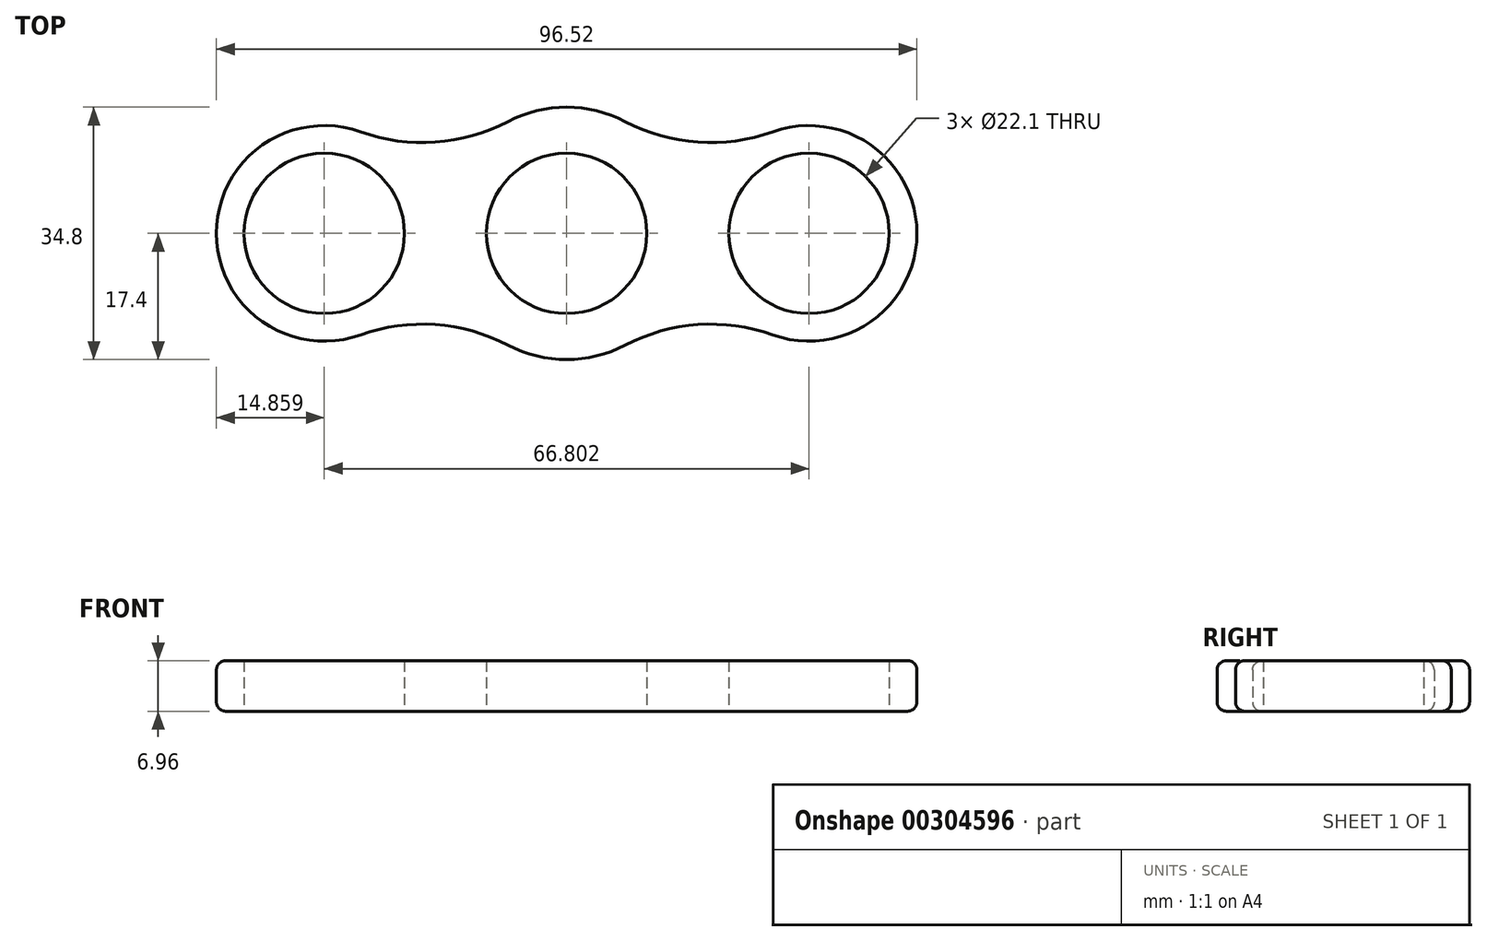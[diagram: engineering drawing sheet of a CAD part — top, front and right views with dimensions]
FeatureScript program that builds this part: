
annotation { "Feature Type Name" : "Feature", "Feature Type Description" : "" }
export const myFeature = defineFeature(function(context is Context, id is Id, definition is map)
    precondition{}
    {
        {
            var Q0;
            Q0=qCreatedBy(makeId("Top.planeOp"),FACE);
            var sketch = newSketch(context, id + "F0", { "sketchPlane" : qUnion([Q0])});
            skCircle(sketch, "E0", {"center": v(0, 0) * mm, "radius": 11.05 * mm});
            skCircle(sketch, "E1", {"center": v(-33.4, 0) * mm, "radius": 11.05 * mm});
            skCircle(sketch, "E2", {"center": v(33.4, 0) * mm, "radius": 11.05 * mm});
            skLineSegment(sketch, "E3.0", {"start": v(27.1, -12.68) * mm, "end": v(27.1, -12.68) * mm});
            skArc(sketch, "E4.0", {"start": v(-8.07, -15.41) * mm, "mid": v(0, -17.4) * mm, "end": v(8.07, -15.41) * mm});
            skArc(sketch, "E5.0", {"start": v(-28.4, 14) * mm, "mid": v(-48.26, 0) * mm, "end": v(-28.4, -14) * mm});
            skArc(sketch, "E6.0", {"start": v(28.4, -14) * mm, "mid": v(48.26, 0) * mm, "end": v(28.4, 14) * mm});
            skArc(sketch, "E7.trimOffspring", {"start": v(8.07, 15.41) * mm, "mid": v(0, 17.4) * mm, "end": v(-8.07, 15.41) * mm});
            skArc(sketch, "E8.filletArc", {"start": v(-28.4, 14) * mm, "mid": v(-18.09, 12.57) * mm, "end": v(-8.07, 15.41) * mm});
            skArc(sketch, "E9.filletArc", {"start": v(-8.07, -15.41) * mm, "mid": v(-18.09, -12.57) * mm, "end": v(-28.4, -14) * mm});
            skArc(sketch, "E10.filletArc", {"start": v(28.4, -14) * mm, "mid": v(18.09, -12.57) * mm, "end": v(8.07, -15.41) * mm});
            skArc(sketch, "E11.filletArc", {"start": v(8.07, 15.41) * mm, "mid": v(18.09, 12.57) * mm, "end": v(28.4, 14) * mm});
            skSolve(sketch);
        }
        {
            var Q0;
            Q0=makeQuery(id+"F0.imprint","IMPRINT",FACE,{"disambiguationData":[TD([[makeQuery(id+"F0.imprint","IMPRINT",EDGE,{"derivedFrom":sQuery(id+"F0.wireOp",EDGE,"E0")}),-1.0]])]});
            extrude(context, id + "F1", {"entities" : qUnion([Q0]), "depth" : 6.96 * mm});
        }
        {
            var Q0;
            Q0=makeQuery(id+"F1.opExtrude","CAP_EDGE",EDGE,{"disambiguationData":[OSD([sQuery(id+"F0.wireOp",EDGE,"E9.filletArc")])],"isStart":false});
            var Q1;
            Q1=makeQuery(id+"F1.opExtrude","CAP_EDGE",EDGE,{"disambiguationData":[OSD([sQuery(id+"F0.wireOp",EDGE,"E5.0")])],"isStart":true});
            fillet(context, id + "F2", {"entities" : qUnion([Q0, Q1]), "radius" : 1.27 * mm, "tangentPropagation" : true, "allowEdgeOverflow" : false});
        }
    });
